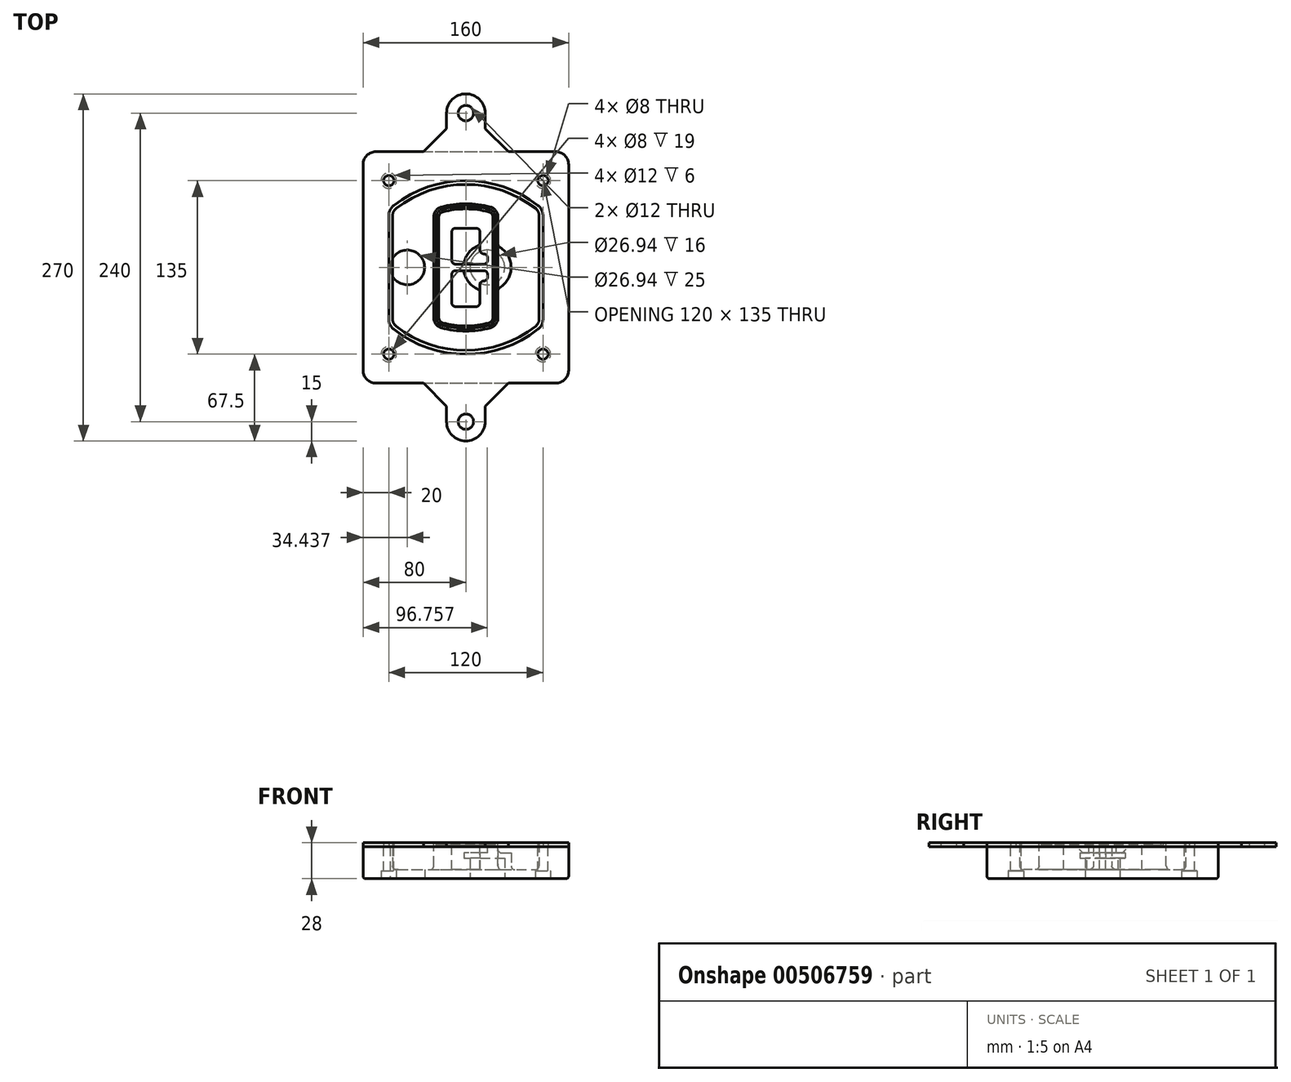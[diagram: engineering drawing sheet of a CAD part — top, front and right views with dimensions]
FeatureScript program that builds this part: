
annotation { "Feature Type Name" : "Feature", "Feature Type Description" : "" }
export const myFeature = defineFeature(function(context is Context, id is Id, definition is map)
    precondition{}
    {
        {
            var Q0;
            Q0=qCreatedBy(makeId("Top.planeOp"),FACE);
            var sketch = newSketch(context, id + "F0", { "sketchPlane" : qUnion([Q0])});
            skPoint(sketch, "E0.rect.middle", {"position": v(0, 0) * mm});
            skLineSegment(sketch, "E1.bottom", {"start": v(-70, -90) * mm, "end": v(70, -90) * mm});
            skLineSegment(sketch, "E1.top", {"start": v(-70, 90) * mm, "end": v(70, 90) * mm});
            skLineSegment(sketch, "E1.left", {"start": v(-80, -80) * mm, "end": v(-80, 80) * mm});
            skLineSegment(sketch, "E1.right", {"start": v(80, -80) * mm, "end": v(80, 80) * mm});
            skLineSegment(sketch, "E2", {"start": v(-80, 90) * mm, "end": v(80, -90) * mm, "construction": true});
            skLineSegment(sketch, "E3", {"start": v(80, 90) * mm, "end": v(-80, -90) * mm, "construction": true});
            skCircle(sketch, "E4", {"center": v(-60, 67.5) * mm, "radius": 4 * mm});
            skCircle(sketch, "E5", {"center": v(60, 67.5) * mm, "radius": 4 * mm});
            skCircle(sketch, "E6", {"center": v(60, -67.5) * mm, "radius": 4 * mm});
            skCircle(sketch, "E7", {"center": v(-60, -67.5) * mm, "radius": 4 * mm});
            skLineSegment(sketch, "E8", {"start": v(-60, 67.5) * mm, "end": v(60, 67.5) * mm, "construction": true});
            skLineSegment(sketch, "E9", {"start": v(60, 67.5) * mm, "end": v(60, -67.5) * mm, "construction": true});
            skLineSegment(sketch, "E10", {"start": v(60, -67.5) * mm, "end": v(-60, -67.5) * mm, "construction": true});
            skLineSegment(sketch, "E11", {"start": v(-60, -67.5) * mm, "end": v(-60, 67.5) * mm, "construction": true});
            skLineSegment(sketch, "E12", {"start": v(-60, 40.3) * mm, "end": v(-60, -40.3) * mm});
            skLineSegment(sketch, "E13", {"start": v(60, 40.3) * mm, "end": v(60, -40.3) * mm});
            skArc(sketch, "E14", {"start": v(56.15, 48.18) * mm, "mid": v(0, 67.5) * mm, "end": v(-56.15, 48.18) * mm});
            skArc(sketch, "E15", {"start": v(-56.15, -48.18) * mm, "mid": v(0, -67.5) * mm, "end": v(56.15, -48.18) * mm});
            skLineSegment(sketch, "E16", {"start": v(-60, 0) * mm, "end": v(60, 0) * mm, "construction": true});
            skPoint(sketch, "E17.visualSharp", {"position": v(-60, -45) * mm});
            skArc(sketch, "E17.filletArc", {"start": v(-60, -40.3) * mm, "mid": v(-58.99, -44.68) * mm, "end": v(-56.15, -48.18) * mm});
            skPoint(sketch, "E18.visualSharp", {"position": v(-60, 45) * mm});
            skArc(sketch, "E18.filletArc", {"start": v(-56.15, 48.18) * mm, "mid": v(-58.99, 44.68) * mm, "end": v(-60, 40.3) * mm});
            skPoint(sketch, "E19.visualSharp", {"position": v(60, 45) * mm});
            skArc(sketch, "E19.filletArc", {"start": v(60, 40.3) * mm, "mid": v(58.99, 44.68) * mm, "end": v(56.15, 48.18) * mm});
            skPoint(sketch, "E20.visualSharp", {"position": v(60, -45) * mm});
            skArc(sketch, "E20.filletArc", {"start": v(56.15, -48.18) * mm, "mid": v(58.99, -44.68) * mm, "end": v(60, -40.3) * mm});
            skPoint(sketch, "E21.visualSharp", {"position": v(-80, 90) * mm});
            skArc(sketch, "E21.filletArc", {"start": v(-70, 90) * mm, "mid": v(-77.07, 87.07) * mm, "end": v(-80, 80) * mm});
            skPoint(sketch, "E22.visualSharp", {"position": v(80, 90) * mm});
            skArc(sketch, "E22.filletArc", {"start": v(80, 80) * mm, "mid": v(77.07, 87.07) * mm, "end": v(70, 90) * mm});
            skPoint(sketch, "E23.visualSharp", {"position": v(80, -90) * mm});
            skArc(sketch, "E23.filletArc", {"start": v(70, -90) * mm, "mid": v(77.07, -87.07) * mm, "end": v(80, -80) * mm});
            skPoint(sketch, "E24.visualSharp", {"position": v(-80, -90) * mm});
            skArc(sketch, "E24.filletArc", {"start": v(-80, -80) * mm, "mid": v(-77.07, -87.07) * mm, "end": v(-70, -90) * mm});
            skArc(sketch, "E25.0", {"start": v(57, 40.3) * mm, "mid": v(56.3, 43.36) * mm, "end": v(54.3, 45.81) * mm});
            skLineSegment(sketch, "E25.1", {"start": v(57, 40.3) * mm, "end": v(57, -40.3) * mm});
            skArc(sketch, "E25.2", {"start": v(54.3, -45.81) * mm, "mid": v(56.3, -43.36) * mm, "end": v(57, -40.3) * mm});
            skArc(sketch, "E25.3", {"start": v(-54.3, -45.81) * mm, "mid": v(0, -64.5) * mm, "end": v(54.3, -45.81) * mm});
            skArc(sketch, "E25.4", {"start": v(-57, -40.3) * mm, "mid": v(-56.3, -43.36) * mm, "end": v(-54.3, -45.81) * mm});
            skArc(sketch, "E25.5", {"start": v(54.3, 45.81) * mm, "mid": v(0, 64.5) * mm, "end": v(-54.3, 45.81) * mm});
            skLineSegment(sketch, "E25.6", {"start": v(-57, 40.3) * mm, "end": v(-57, -40.3) * mm});
            skArc(sketch, "E25.7", {"start": v(-54.3, 45.81) * mm, "mid": v(-56.3, 43.36) * mm, "end": v(-57, 40.3) * mm});
            skArc(sketch, "E26.0", {"start": v(-58.62, 51.33) * mm, "mid": v(-62.58, 46.43) * mm, "end": v(-64, 40.3) * mm});
            skArc(sketch, "E26.1", {"start": v(58.62, 51.33) * mm, "mid": v(0, 71.5) * mm, "end": v(-58.62, 51.33) * mm});
            skArc(sketch, "E26.2", {"start": v(64, 40.3) * mm, "mid": v(62.58, 46.43) * mm, "end": v(58.62, 51.33) * mm});
            skLineSegment(sketch, "E26.3", {"start": v(64, 40.3) * mm, "end": v(64, -40.3) * mm});
            skArc(sketch, "E26.4", {"start": v(58.62, -51.33) * mm, "mid": v(62.58, -46.43) * mm, "end": v(64, -40.3) * mm});
            skLineSegment(sketch, "E26.5", {"start": v(-64, 40.3) * mm, "end": v(-64, -40.3) * mm});
            skArc(sketch, "E26.6", {"start": v(-58.62, -51.33) * mm, "mid": v(0, -71.5) * mm, "end": v(58.62, -51.33) * mm});
            skArc(sketch, "E26.7", {"start": v(-64, -40.3) * mm, "mid": v(-62.58, -46.43) * mm, "end": v(-58.62, -51.33) * mm});
            skSolve(sketch);
        }
        {
            var Q0;
            Q0=makeQuery(id+"F0.imprint","IMPRINT",FACE,{"disambiguationData":[TD([[makeQuery(id+"F0.imprint","IMPRINT",EDGE,{"derivedFrom":sQuery(id+"F0.wireOp",EDGE,"E1.bottom")}),1.0]])]});
            var Q1;
            Q1=makeQuery(id+"F0.imprint","IMPRINT",FACE,{"disambiguationData":[TD([[makeQuery(id+"F0.imprint","IMPRINT",EDGE,{"derivedFrom":sQuery(id+"F0.wireOp",EDGE,"E12")}),1.0]])]});
            var Q2;
            Q2=makeQuery(id+"F0.imprint","IMPRINT",FACE,{"disambiguationData":[TD([[makeQuery(id+"F0.imprint","IMPRINT",EDGE,{"derivedFrom":sQuery(id+"F0.wireOp",EDGE,"E25.0")}),1.0]])]});
            var Q3;
            Q3=makeQuery(id+"F0.imprint","IMPRINT",FACE,{"disambiguationData":[TD([[makeQuery(id+"F0.imprint","IMPRINT",EDGE,{"derivedFrom":sQuery(id+"F0.wireOp",EDGE,"E12")}),-1.0]])]});
            extrude(context, id + "F1", {"entities" : qUnion([Q0, Q1, Q2, Q3]), "oppositeDirection" : true, "depth" : 25 * mm});
        }
        {
            var Q0;
            Q0=makeQuery(id+"F0.imprint","IMPRINT",FACE,{"disambiguationData":[TD([[makeQuery(id+"F0.imprint","IMPRINT",EDGE,{"derivedFrom":sQuery(id+"F0.wireOp",EDGE,"E12")}),1.0]])]});
            extrude(context, id + "F2", {"entities" : qUnion([Q0]), "operationType" : NewBodyOperationType.ADD, "depth" : 3 * mm});
        }
        {
            var Q0;
            Q0=makeQuery(id+"F0.imprint","IMPRINT",FACE,{"disambiguationData":[TD([[makeQuery(id+"F0.imprint","IMPRINT",EDGE,{"derivedFrom":sQuery(id+"F0.wireOp",EDGE,"E25.0")}),1.0]])]});
            extrude(context, id + "F3", {"entities" : qUnion([Q0]), "operationType" : NewBodyOperationType.REMOVE, "oppositeDirection" : true, "depth" : 18 * mm});
        }
        {
            var Q0;
            Q0=makeQuery(id+"F2.opExtrude","CAP_FACE",FACE,{"disambiguationData":[OSD([sQuery(id+"F0.wireOp",EDGE,"E12"),sQuery(id+"F0.wireOp",EDGE,"E13"),sQuery(id+"F0.wireOp",EDGE,"E14"),sQuery(id+"F0.wireOp",EDGE,"E15"),sQuery(id+"F0.wireOp",EDGE,"E17.filletArc"),sQuery(id+"F0.wireOp",EDGE,"E18.filletArc"),sQuery(id+"F0.wireOp",EDGE,"E19.filletArc"),sQuery(id+"F0.wireOp",EDGE,"E20.filletArc"),sQuery(id+"F0.wireOp",EDGE,"E25.0"),sQuery(id+"F0.wireOp",EDGE,"E25.1"),sQuery(id+"F0.wireOp",EDGE,"E25.2"),sQuery(id+"F0.wireOp",EDGE,"E25.3"),sQuery(id+"F0.wireOp",EDGE,"E25.4"),sQuery(id+"F0.wireOp",EDGE,"E25.5"),sQuery(id+"F0.wireOp",EDGE,"E25.6"),sQuery(id+"F0.wireOp",EDGE,"E25.7")])],"isStart":false});
            var sketch = newSketch(context, id + "F4", { "sketchPlane" : qUnion([Q0])});
            skArc(sketch, "E27.0", {"start": v(-19.08, -46.97) * mm, "mid": v(0, -49.5) * mm, "end": v(19.08, -46.97) * mm});
            skArc(sketch, "E28.0", {"start": v(19.08, 46.97) * mm, "mid": v(0, 49.5) * mm, "end": v(-19.08, 46.97) * mm});
            skLineSegment(sketch, "E29", {"start": v(-25, 39.25) * mm, "end": v(-25, -39.25) * mm});
            skLineSegment(sketch, "E30", {"start": v(25, 39.25) * mm, "end": v(25, -39.25) * mm});
            skLineSegment(sketch, "E31", {"start": v(-25, 45.1) * mm, "end": v(25, 45.1) * mm, "construction": true});
            skLineSegment(sketch, "E32", {"start": v(-25, -45.1) * mm, "end": v(25, -45.1) * mm, "construction": true});
            skPoint(sketch, "E33.visualSharp", {"position": v(-25, 45.1) * mm});
            skArc(sketch, "E33.filletArc", {"start": v(-19.08, 46.97) * mm, "mid": v(-23.35, 44.11) * mm, "end": v(-25, 39.25) * mm});
            skPoint(sketch, "E34.visualSharp", {"position": v(25, 45.1) * mm});
            skArc(sketch, "E34.filletArc", {"start": v(25, 39.25) * mm, "mid": v(23.35, 44.11) * mm, "end": v(19.08, 46.97) * mm});
            skPoint(sketch, "E35.visualSharp", {"position": v(25, -45.1) * mm});
            skArc(sketch, "E35.filletArc", {"start": v(19.08, -46.97) * mm, "mid": v(23.35, -44.11) * mm, "end": v(25, -39.25) * mm});
            skPoint(sketch, "E36.visualSharp", {"position": v(-25, -45.1) * mm});
            skArc(sketch, "E36.filletArc", {"start": v(-25, -39.25) * mm, "mid": v(-23.35, -44.11) * mm, "end": v(-19.08, -46.97) * mm});
            skArc(sketch, "E37.0", {"start": v(54.3, 45.81) * mm, "mid": v(0, 64.5) * mm, "end": v(-54.3, 45.81) * mm});
            skArc(sketch, "E37.1", {"start": v(-54.3, 45.81) * mm, "mid": v(-56.3, 43.36) * mm, "end": v(-57, 40.3) * mm});
            skLineSegment(sketch, "E37.2", {"start": v(-57, 40.3) * mm, "end": v(-57, -40.3) * mm});
            skArc(sketch, "E37.3", {"start": v(-57, -40.3) * mm, "mid": v(-56.3, -43.36) * mm, "end": v(-54.3, -45.81) * mm});
            skArc(sketch, "E37.4", {"start": v(-54.3, -45.81) * mm, "mid": v(0, -64.5) * mm, "end": v(54.3, -45.81) * mm});
            skArc(sketch, "E37.5", {"start": v(54.3, -45.81) * mm, "mid": v(56.3, -43.36) * mm, "end": v(57, -40.3) * mm});
            skLineSegment(sketch, "E37.6", {"start": v(57, 40.3) * mm, "end": v(57, -40.3) * mm});
            skArc(sketch, "E37.7", {"start": v(57, 40.3) * mm, "mid": v(56.3, 43.36) * mm, "end": v(54.3, 45.81) * mm});
            skLineSegment(sketch, "E38.0", {"start": v(23, 39.25) * mm, "end": v(23, -39.25) * mm});
            skArc(sketch, "E38.1", {"start": v(18.56, -45.04) * mm, "mid": v(21.76, -42.9) * mm, "end": v(23, -39.25) * mm});
            skArc(sketch, "E38.2", {"start": v(-18.56, -45.04) * mm, "mid": v(0, -47.5) * mm, "end": v(18.56, -45.04) * mm});
            skArc(sketch, "E38.3", {"start": v(-23, -39.25) * mm, "mid": v(-21.76, -42.9) * mm, "end": v(-18.56, -45.04) * mm});
            skLineSegment(sketch, "E38.4", {"start": v(-23, 39.25) * mm, "end": v(-23, -39.25) * mm});
            skArc(sketch, "E38.5", {"start": v(23, 39.25) * mm, "mid": v(21.76, 42.9) * mm, "end": v(18.56, 45.04) * mm});
            skArc(sketch, "E38.6", {"start": v(-18.56, 45.04) * mm, "mid": v(-21.76, 42.9) * mm, "end": v(-23, 39.25) * mm});
            skArc(sketch, "E38.7", {"start": v(18.56, 45.04) * mm, "mid": v(0, 47.5) * mm, "end": v(-18.56, 45.04) * mm});
            skArc(sketch, "E39.0", {"start": v(21, 39.25) * mm, "mid": v(20.18, 41.68) * mm, "end": v(18.04, 43.1) * mm});
            skLineSegment(sketch, "E39.1", {"start": v(21, 39.25) * mm, "end": v(21, -39.25) * mm});
            skArc(sketch, "E39.2", {"start": v(18.04, -43.1) * mm, "mid": v(20.18, -41.68) * mm, "end": v(21, -39.25) * mm});
            skArc(sketch, "E39.3", {"start": v(-18.04, -43.1) * mm, "mid": v(0, -45.5) * mm, "end": v(18.04, -43.1) * mm});
            skArc(sketch, "E39.4", {"start": v(-21, -39.25) * mm, "mid": v(-20.18, -41.68) * mm, "end": v(-18.04, -43.1) * mm});
            skArc(sketch, "E39.5", {"start": v(18.04, 43.1) * mm, "mid": v(0, 45.5) * mm, "end": v(-18.04, 43.1) * mm});
            skLineSegment(sketch, "E39.6", {"start": v(-21, 39.25) * mm, "end": v(-21, -39.25) * mm});
            skArc(sketch, "E39.7", {"start": v(-18.04, 43.1) * mm, "mid": v(-20.18, 41.68) * mm, "end": v(-21, 39.25) * mm});
            skLineSegment(sketch, "E40", {"start": v(-25, 0) * mm, "end": v(25, 0) * mm, "construction": true});
            skLineSegment(sketch, "E41", {"start": v(-11, 5.5) * mm, "end": v(-11, 27.5) * mm});
            skLineSegment(sketch, "E42", {"start": v(-8, 30.5) * mm, "end": v(8, 30.5) * mm});
            skLineSegment(sketch, "E43", {"start": v(11, 27.5) * mm, "end": v(11, 13.5) * mm});
            skLineSegment(sketch, "E44", {"start": v(14, 10.5) * mm, "end": v(14, 10.5) * mm});
            skLineSegment(sketch, "E45", {"start": v(17, 7.5) * mm, "end": v(17, 5.5) * mm});
            skLineSegment(sketch, "E46", {"start": v(14, 2.5) * mm, "end": v(-8, 2.5) * mm});
            skPoint(sketch, "E47.visualSharp", {"position": v(-11, 30.5) * mm});
            skArc(sketch, "E47.filletArc", {"start": v(-8, 30.5) * mm, "mid": v(-10.12, 29.62) * mm, "end": v(-11, 27.5) * mm});
            skPoint(sketch, "E48.visualSharp", {"position": v(11, 30.5) * mm});
            skArc(sketch, "E48.filletArc", {"start": v(11, 27.5) * mm, "mid": v(10.12, 29.62) * mm, "end": v(8, 30.5) * mm});
            skPoint(sketch, "E49.visualSharp", {"position": v(11, 10.5) * mm});
            skArc(sketch, "E49.filletArc", {"start": v(11, 13.5) * mm, "mid": v(11.88, 11.38) * mm, "end": v(14, 10.5) * mm});
            skPoint(sketch, "E50.visualSharp", {"position": v(17, 10.5) * mm});
            skArc(sketch, "E50.filletArc", {"start": v(17, 7.5) * mm, "mid": v(16.12, 9.62) * mm, "end": v(14, 10.5) * mm});
            skPoint(sketch, "E51.visualSharp", {"position": v(17, 2.5) * mm});
            skArc(sketch, "E51.filletArc", {"start": v(14, 2.5) * mm, "mid": v(16.12, 3.38) * mm, "end": v(17, 5.5) * mm});
            skPoint(sketch, "E52.visualSharp", {"position": v(-11, 2.5) * mm});
            skArc(sketch, "E52.filletArc", {"start": v(-11, 5.5) * mm, "mid": v(-10.12, 3.38) * mm, "end": v(-8, 2.5) * mm});
            skLineSegment(sketch, "E53.0.MirrorCS", {"start": v(14, -2.5) * mm, "end": v(-8, -2.5) * mm});
            skArc(sketch, "E54.0.MirrorCS", {"start": v(-11, -5.5) * mm, "mid": v(-10.12, -3.38) * mm, "end": v(-8, -2.5) * mm});
            skLineSegment(sketch, "E55.0.MirrorCS", {"start": v(-11, -5.5) * mm, "end": v(-11, -27.5) * mm});
            skArc(sketch, "E56.0.MirrorCS", {"start": v(-8, -30.5) * mm, "mid": v(-10.12, -29.62) * mm, "end": v(-11, -27.5) * mm});
            skLineSegment(sketch, "E57.0.MirrorCS", {"start": v(-8, -30.5) * mm, "end": v(8, -30.5) * mm});
            skArc(sketch, "E58.0.MirrorCS", {"start": v(11, -27.5) * mm, "mid": v(10.12, -29.62) * mm, "end": v(8, -30.5) * mm});
            skLineSegment(sketch, "E59.0.MirrorCS", {"start": v(11, -27.5) * mm, "end": v(11, -13.5) * mm});
            skArc(sketch, "E60.0.MirrorCS", {"start": v(11, -13.5) * mm, "mid": v(11.88, -11.38) * mm, "end": v(14, -10.5) * mm});
            skArc(sketch, "E61.0.MirrorCS", {"start": v(17, -7.5) * mm, "mid": v(16.12, -9.62) * mm, "end": v(14, -10.5) * mm});
            skLineSegment(sketch, "E62.0.MirrorCS", {"start": v(17, -7.5) * mm, "end": v(17, -5.5) * mm});
            skArc(sketch, "E63.0.MirrorCS", {"start": v(14, -2.5) * mm, "mid": v(16.12, -3.38) * mm, "end": v(17, -5.5) * mm});
            skSolve(sketch);
        }
        {
            var Q0;
            Q0=makeQuery(id+"F4.imprint","IMPRINT",FACE,{"disambiguationData":[TD([[makeQuery(id+"F4.imprint","IMPRINT",EDGE,{"derivedFrom":sQuery(id+"F4.wireOp",EDGE,"E27.0")}),1.0]])]});
            var Q1;
            Q1=makeQuery(id+"F4.imprint","IMPRINT",FACE,{"disambiguationData":[TD([[makeQuery(id+"F4.imprint","IMPRINT",EDGE,{"derivedFrom":sQuery(id+"F4.wireOp",EDGE,"E38.0")}),-1.0]])]});
            var Q2;
            Q2=makeQuery(id+"F4.imprint","IMPRINT",FACE,{"disambiguationData":[TD([[makeQuery(id+"F4.imprint","IMPRINT",EDGE,{"derivedFrom":sQuery(id+"F4.wireOp",EDGE,"E39.0")}),1.0]])]});
            extrude(context, id + "F5", {"entities" : qUnion([Q0, Q1, Q2]), "operationType" : NewBodyOperationType.ADD, "endBound" : BoundingType.UP_TO_NEXT, "oppositeDirection" : true, "depth" : 25 * mm});
        }
        {
            var Q0;
            Q0=makeQuery(id+"F4.imprint","IMPRINT",FACE,{"disambiguationData":[TD([[makeQuery(id+"F4.imprint","IMPRINT",EDGE,{"derivedFrom":sQuery(id+"F4.wireOp",EDGE,"E38.0")}),-1.0]])]});
            extrude(context, id + "F6", {"entities" : qUnion([Q0]), "operationType" : NewBodyOperationType.REMOVE, "oppositeDirection" : true, "depth" : 2 * mm});
        }
        {
            var Q0;
            Q0=makeQuery(id+"F1.opExtrude","CAP_FACE",FACE,{"disambiguationData":[OSD([sQuery(id+"F0.wireOp",EDGE,"E1.bottom"),sQuery(id+"F0.wireOp",EDGE,"E1.top"),sQuery(id+"F0.wireOp",EDGE,"E1.left"),sQuery(id+"F0.wireOp",EDGE,"E1.right"),sQuery(id+"F0.wireOp",EDGE,"E4"),sQuery(id+"F0.wireOp",EDGE,"E5"),sQuery(id+"F0.wireOp",EDGE,"E6"),sQuery(id+"F0.wireOp",EDGE,"E7"),sQuery(id+"F0.wireOp",EDGE,"E21.filletArc"),sQuery(id+"F0.wireOp",EDGE,"E22.filletArc"),sQuery(id+"F0.wireOp",EDGE,"E23.filletArc"),sQuery(id+"F0.wireOp",EDGE,"E24.filletArc")])],"isStart":false});
            var sketch = newSketch(context, id + "F7", { "sketchPlane" : qUnion([Q0])});
            skCircle(sketch, "E64", {"center": v(16.76, 0) * mm, "radius": 13.47 * mm});
            skCircle(sketch, "E65", {"center": v(-45.56, 0) * mm, "radius": 13.47 * mm});
            skLineSegment(sketch, "E66", {"start": v(80, 0) * mm, "end": v(-80, 0) * mm});
            skCircle(sketch, "E67", {"center": v(16.76, 0) * mm, "radius": 18.47 * mm});
            skCircle(sketch, "E68", {"center": v(60, -67.5) * mm, "radius": 6 * mm});
            skCircle(sketch, "E69", {"center": v(-60, -67.5) * mm, "radius": 6 * mm});
            skCircle(sketch, "E70", {"center": v(-60, 67.5) * mm, "radius": 6 * mm});
            skCircle(sketch, "E71", {"center": v(60, 67.5) * mm, "radius": 6 * mm});
            skSolve(sketch);
        }
        {
            var Q0;
            {var subQ1=sQuery(id+"F7.wireOp",EDGE,"E66");var subQ4=sQuery(id+"F7.wireOp",EDGE,"E64");var subQ6=makeQuery(id+"F7.imprint","INTERSECT",VERTEX,{"disambiguationData":[OD(0.0)],"derivedFrom":[subQ4,subQ1]});Q0=makeQuery(id+"F7.imprint","IMPRINT",FACE,{"disambiguationData":[TD([[makeQuery(id+"F7.imprint","IMPRINT",EDGE,{"disambiguationData":[TD([[subQ6,-1.0]])],"derivedFrom":subQ4}),-1.0]])]});}
            var Q1;
            {var subQ0=sQuery(id+"F7.wireOp",EDGE,"E66");var subQ1=sQuery(id+"F7.wireOp",EDGE,"E64");var subQ3=makeQuery(id+"F7.imprint","INTERSECT",VERTEX,{"disambiguationData":[OD(0.0)],"derivedFrom":[subQ1,subQ0]});Q1=makeQuery(id+"F7.imprint","IMPRINT",FACE,{"disambiguationData":[TD([[makeQuery(id+"F7.imprint","IMPRINT",EDGE,{"disambiguationData":[TD([[subQ3,-1.0]])],"derivedFrom":subQ1}),1.0]])]});}
            var Q2;
            {var subQ0=sQuery(id+"F7.wireOp",EDGE,"E66");var subQ1=sQuery(id+"F7.wireOp",EDGE,"E64");var subQ3=makeQuery(id+"F7.imprint","INTERSECT",VERTEX,{"disambiguationData":[OD(0.0)],"derivedFrom":[subQ1,subQ0]});Q2=makeQuery(id+"F7.imprint","IMPRINT",FACE,{"disambiguationData":[TD([[makeQuery(id+"F7.imprint","IMPRINT",EDGE,{"disambiguationData":[TD([[subQ3,1.0]])],"derivedFrom":subQ1}),1.0]])]});}
            var Q3;
            {var subQ1=sQuery(id+"F7.wireOp",EDGE,"E66");var subQ4=sQuery(id+"F7.wireOp",EDGE,"E64");var subQ6=makeQuery(id+"F7.imprint","INTERSECT",VERTEX,{"disambiguationData":[OD(0.0)],"derivedFrom":[subQ4,subQ1]});Q3=makeQuery(id+"F7.imprint","IMPRINT",FACE,{"disambiguationData":[TD([[makeQuery(id+"F7.imprint","IMPRINT",EDGE,{"disambiguationData":[TD([[subQ6,1.0]])],"derivedFrom":subQ4}),-1.0]])]});}
            extrude(context, id + "F8", {"entities" : qUnion([Q0, Q1, Q2, Q3]), "operationType" : NewBodyOperationType.ADD, "oppositeDirection" : true, "depth" : 20 * mm});
        }
        {
            var Q0;
            {var subQ0=sQuery(id+"F7.wireOp",EDGE,"E66");var subQ1=sQuery(id+"F7.wireOp",EDGE,"E64");var subQ3=makeQuery(id+"F7.imprint","INTERSECT",VERTEX,{"disambiguationData":[OD(0.0)],"derivedFrom":[subQ1,subQ0]});Q0=makeQuery(id+"F7.imprint","IMPRINT",FACE,{"disambiguationData":[TD([[makeQuery(id+"F7.imprint","IMPRINT",EDGE,{"disambiguationData":[TD([[subQ3,-1.0]])],"derivedFrom":subQ1}),1.0]])]});}
            var Q1;
            {var subQ0=sQuery(id+"F7.wireOp",EDGE,"E66");var subQ1=sQuery(id+"F7.wireOp",EDGE,"E64");var subQ3=makeQuery(id+"F7.imprint","INTERSECT",VERTEX,{"disambiguationData":[OD(0.0)],"derivedFrom":[subQ1,subQ0]});Q1=makeQuery(id+"F7.imprint","IMPRINT",FACE,{"disambiguationData":[TD([[makeQuery(id+"F7.imprint","IMPRINT",EDGE,{"disambiguationData":[TD([[subQ3,1.0]])],"derivedFrom":subQ1}),1.0]])]});}
            extrude(context, id + "F9", {"entities" : qUnion([Q0, Q1]), "operationType" : NewBodyOperationType.REMOVE, "oppositeDirection" : true, "depth" : 16 * mm});
        }
        {
            var Q0;
            {var subQ0=sQuery(id+"F7.wireOp",EDGE,"E66");var subQ1=sQuery(id+"F7.wireOp",EDGE,"E65");var subQ3=makeQuery(id+"F7.imprint","INTERSECT",VERTEX,{"disambiguationData":[OD(0.0)],"derivedFrom":[subQ1,subQ0]});Q0=makeQuery(id+"F7.imprint","IMPRINT",FACE,{"disambiguationData":[TD([[makeQuery(id+"F7.imprint","IMPRINT",EDGE,{"disambiguationData":[TD([[subQ3,-1.0]])],"derivedFrom":subQ1}),1.0]])]});}
            var Q1;
            {var subQ0=sQuery(id+"F7.wireOp",EDGE,"E66");var subQ1=sQuery(id+"F7.wireOp",EDGE,"E65");var subQ3=makeQuery(id+"F7.imprint","INTERSECT",VERTEX,{"disambiguationData":[OD(0.0)],"derivedFrom":[subQ1,subQ0]});Q1=makeQuery(id+"F7.imprint","IMPRINT",FACE,{"disambiguationData":[TD([[makeQuery(id+"F7.imprint","IMPRINT",EDGE,{"disambiguationData":[TD([[subQ3,1.0]])],"derivedFrom":subQ1}),1.0]])]});}
            extrude(context, id + "F10", {"entities" : qUnion([Q0, Q1]), "operationType" : NewBodyOperationType.REMOVE, "oppositeDirection" : true, "depth" : 25 * mm});
        }
        {
            var Q0;
            Q0=makeQuery(id+"F7.imprint","IMPRINT",FACE,{"disambiguationData":[TD([[makeQuery(id+"F7.imprint","IMPRINT",EDGE,{"derivedFrom":sQuery(id+"F7.wireOp",EDGE,"E68")}),1.0]])]});
            var Q1;
            Q1=makeQuery(id+"F7.imprint","IMPRINT",FACE,{"disambiguationData":[TD([[makeQuery(id+"F7.imprint","IMPRINT",EDGE,{"derivedFrom":makeQuery(id+"F1.opExtrude","CAP_EDGE",EDGE,{"disambiguationData":[OSD([sQuery(id+"F0.wireOp",EDGE,"E5")])],"isStart":false})}),-1.0]])]});
            var Q2;
            Q2=makeQuery(id+"F7.imprint","IMPRINT",FACE,{"disambiguationData":[TD([[makeQuery(id+"F7.imprint","IMPRINT",EDGE,{"derivedFrom":sQuery(id+"F7.wireOp",EDGE,"E69")}),1.0]])]});
            var Q3;
            Q3=makeQuery(id+"F7.imprint","IMPRINT",FACE,{"disambiguationData":[TD([[makeQuery(id+"F7.imprint","IMPRINT",EDGE,{"derivedFrom":makeQuery(id+"F1.opExtrude","CAP_EDGE",EDGE,{"disambiguationData":[OSD([sQuery(id+"F0.wireOp",EDGE,"E4")])],"isStart":false})}),-1.0]])]});
            var Q4;
            Q4=makeQuery(id+"F7.imprint","IMPRINT",FACE,{"disambiguationData":[TD([[makeQuery(id+"F7.imprint","IMPRINT",EDGE,{"derivedFrom":sQuery(id+"F7.wireOp",EDGE,"E70")}),1.0]])]});
            var Q5;
            Q5=makeQuery(id+"F7.imprint","IMPRINT",FACE,{"disambiguationData":[TD([[makeQuery(id+"F7.imprint","IMPRINT",EDGE,{"derivedFrom":makeQuery(id+"F1.opExtrude","CAP_EDGE",EDGE,{"disambiguationData":[OSD([sQuery(id+"F0.wireOp",EDGE,"E7")])],"isStart":false})}),-1.0]])]});
            var Q6;
            Q6=makeQuery(id+"F7.imprint","IMPRINT",FACE,{"disambiguationData":[TD([[makeQuery(id+"F7.imprint","IMPRINT",EDGE,{"derivedFrom":sQuery(id+"F7.wireOp",EDGE,"E71")}),1.0]])]});
            var Q7;
            Q7=makeQuery(id+"F7.imprint","IMPRINT",FACE,{"disambiguationData":[TD([[makeQuery(id+"F7.imprint","IMPRINT",EDGE,{"derivedFrom":makeQuery(id+"F1.opExtrude","CAP_EDGE",EDGE,{"disambiguationData":[OSD([sQuery(id+"F0.wireOp",EDGE,"E6")])],"isStart":false})}),-1.0]])]});
            extrude(context, id + "F11", {"entities" : qUnion([Q0, Q1, Q2, Q3, Q4, Q5, Q6, Q7]), "operationType" : NewBodyOperationType.REMOVE, "oppositeDirection" : true, "depth" : 6 * mm});
        }
        {
            var Q0;
            Q0=makeQuery(id+"F9.boolean.opBoolean","COPY",FACE,{"derivedFrom":makeQuery(id+"F9.opExtrude","CAP_FACE",FACE,{"disambiguationData":[OSD([sQuery(id+"F7.wireOp",EDGE,"E64")])],"isStart":false})});
            var sketch = newSketch(context, id + "F12", { "sketchPlane" : qUnion([Q0])});
            skArc(sketch, "E72.0", {"start": v(11, 17.55) * mm, "mid": v(2.57, 11.82) * mm, "end": v(-1.54, 2.5) * mm});
            skArc(sketch, "E72.1", {"start": v(-1.54, -2.5) * mm, "mid": v(2.57, -11.82) * mm, "end": v(11, -17.55) * mm});
            skLineSegment(sketch, "E73", {"start": v(-1.54, -2.5) * mm, "end": v(14, -2.5) * mm});
            skLineSegment(sketch, "E74.0", {"start": v(14, 2.5) * mm, "end": v(-1.54, 2.5) * mm});
            skArc(sketch, "E74.1", {"start": v(14, 2.5) * mm, "mid": v(16.12, 3.38) * mm, "end": v(17, 5.5) * mm});
            skLineSegment(sketch, "E74.2", {"start": v(17, 7.5) * mm, "end": v(17, 5.5) * mm});
            skArc(sketch, "E74.3", {"start": v(17, 7.5) * mm, "mid": v(16.12, 9.62) * mm, "end": v(14, 10.5) * mm});
            skArc(sketch, "E74.4", {"start": v(11, 13.5) * mm, "mid": v(11.88, 11.38) * mm, "end": v(14, 10.5) * mm});
            skLineSegment(sketch, "E74.5", {"start": v(11, 17.55) * mm, "end": v(11, 13.5) * mm});
            skLineSegment(sketch, "E74.7", {"start": v(14, -2.5) * mm, "end": v(-1.54, -2.5) * mm});
            skArc(sketch, "E74.8", {"start": v(14, -2.5) * mm, "mid": v(16.12, -3.38) * mm, "end": v(17, -5.5) * mm});
            skLineSegment(sketch, "E74.9", {"start": v(17, -7.5) * mm, "end": v(17, -5.5) * mm});
            skArc(sketch, "E74.10", {"start": v(17, -7.5) * mm, "mid": v(16.12, -9.62) * mm, "end": v(14, -10.5) * mm});
            skArc(sketch, "E74.11", {"start": v(11, -13.5) * mm, "mid": v(11.88, -11.38) * mm, "end": v(14, -10.5) * mm});
            skLineSegment(sketch, "E74.12", {"start": v(11, -17.55) * mm, "end": v(11, -13.5) * mm});
            skPoint(sketch, "E75.orphan", {"position": v(11, -27.5) * mm});
            skPoint(sketch, "E76.orphan", {"position": v(-8, -2.5) * mm});
            skPoint(sketch, "E77.orphan", {"position": v(-8, 2.5) * mm});
            skPoint(sketch, "E78.orphan", {"position": v(11, 27.5) * mm});
            skSolve(sketch);
        }
        {
            var Q0;
            {var subQ7=sQuery(id+"F12.wireOp",EDGE,"E72.0");var subQ14=sQuery(id+"F12.wireOp",EDGE,"E72.1");var subQ16=sQuery(id+"F12.wireOp",EDGE,"E74.1");var subQ18=sQuery(id+"F12.wireOp",EDGE,"E74.8");Q0=qUnion([makeQuery(id+"F12.imprint","IMPRINT",FACE,{"disambiguationData":[TD([[makeQuery(id+"F12.imprint","IMPRINT",EDGE,{"derivedFrom":subQ7}),1.0]])]}),makeQuery(id+"F12.imprint","IMPRINT",FACE,{"disambiguationData":[TD([[makeQuery(id+"F12.imprint","IMPRINT",EDGE,{"derivedFrom":subQ14}),1.0]])]}),makeQuery(id+"F12.imprint","IMPRINT",FACE,{"disambiguationData":[TD([[makeQuery(id+"F12.imprint","IMPRINT",EDGE,{"derivedFrom":subQ16}),1.0]])]}),makeQuery(id+"F12.imprint","IMPRINT",FACE,{"disambiguationData":[TD([[makeQuery(id+"F12.imprint","IMPRINT",EDGE,{"derivedFrom":subQ18}),-1.0]])]})]);}
            var Q1;
            Q1=makeQuery(id+"F5.boolean.opBoolean","SPLIT",FACE,{"disambiguationData":[TD([makeQuery(id+"F5.opExtrude","SWEPT_FACE",FACE,{"disambiguationData":[OSD([sQuery(id+"F4.wireOp",EDGE,"E41")])]})])],"derivedFrom":makeQuery(id+"F3.boolean.opBoolean","COPY",FACE,{"derivedFrom":makeQuery(id+"F3.opExtrude","CAP_FACE",FACE,{"disambiguationData":[OSD([sQuery(id+"F0.wireOp",EDGE,"E25.0"),sQuery(id+"F0.wireOp",EDGE,"E25.1"),sQuery(id+"F0.wireOp",EDGE,"E25.2"),sQuery(id+"F0.wireOp",EDGE,"E25.3"),sQuery(id+"F0.wireOp",EDGE,"E25.4"),sQuery(id+"F0.wireOp",EDGE,"E25.5"),sQuery(id+"F0.wireOp",EDGE,"E25.6"),sQuery(id+"F0.wireOp",EDGE,"E25.7")])],"isStart":false})})});
            extrude(context, id + "F13", {"entities" : qUnion([Q0]), "operationType" : NewBodyOperationType.REMOVE, "endBound" : BoundingType.UP_TO_SURFACE, "endBoundEntityFace" : qUnion([Q1]), "depth" : 25 * mm});
        }
        {
            var Q0;
            Q0=makeQuery(id+"F3.boolean.opBoolean","COPY",EDGE,{"derivedFrom":makeQuery(id+"F3.opExtrude","CAP_EDGE",EDGE,{"disambiguationData":[OSD([sQuery(id+"F0.wireOp",EDGE,"E25.6")])],"isStart":false})});
            var Q1;
            Q1=makeQuery(id+"F8.boolean.opBoolean","INTERSECT",EDGE,{"derivedFrom":[makeQuery(id+"F5.opExtrude","SWEPT_FACE",FACE,{"disambiguationData":[OSD([sQuery(id+"F4.wireOp",EDGE,"E30")])]}),makeQuery(id+"F8.opExtrude","CAP_FACE",FACE,{"disambiguationData":[OSD([sQuery(id+"F7.wireOp",EDGE,"E67")])],"isStart":false})]});
            var Q2;
            Q2=makeQuery(id+"F8.boolean.opBoolean","INTERSECT",EDGE,{"disambiguationData":[OD(1.0)],"derivedFrom":[makeQuery(id+"F5.opExtrude","SWEPT_FACE",FACE,{"disambiguationData":[OSD([sQuery(id+"F4.wireOp",EDGE,"E30")])]}),makeQuery(id+"F8.opExtrude","SWEPT_FACE",FACE,{"disambiguationData":[OSD([sQuery(id+"F7.wireOp",EDGE,"E67")])]})]});
            var Q3;
            {var subQ0=sQuery(id+"F4.wireOp",EDGE,"E30");Q3=makeQuery(id+"F8.boolean.opBoolean","SPLIT",EDGE,{"disambiguationData":[TD([makeQuery(id+"F5.opExtrude","SWEPT_FACE",FACE,{"disambiguationData":[OSD([sQuery(id+"F4.wireOp",EDGE,"E35.filletArc")])]})])],"derivedFrom":makeQuery(id+"F5.opExtrude","CAP_EDGE",EDGE,{"disambiguationData":[OSD([subQ0])],"isStart":false})});}
            var Q4;
            {var subQ0=sQuery(id+"F0.wireOp",EDGE,"E25.7");var subQ1=sQuery(id+"F0.wireOp",EDGE,"E25.1");var subQ2=sQuery(id+"F0.wireOp",EDGE,"E25.6");var subQ3=sQuery(id+"F0.wireOp",EDGE,"E25.5");var subQ4=sQuery(id+"F0.wireOp",EDGE,"E25.4");var subQ5=sQuery(id+"F0.wireOp",EDGE,"E25.0");var subQ6=sQuery(id+"F0.wireOp",EDGE,"E25.2");var subQ7=sQuery(id+"F0.wireOp",EDGE,"E25.3");Q4=makeQuery(id+"F8.boolean.opBoolean","INTERSECT",EDGE,{"derivedFrom":[makeQuery(id+"F5.boolean.opBoolean","SPLIT",FACE,{"disambiguationData":[TD([makeQuery(id+"F2.opExtrude","SWEPT_FACE",FACE,{"disambiguationData":[OSD([subQ5])]})])],"derivedFrom":makeQuery(id+"F3.boolean.opBoolean","COPY",FACE,{"derivedFrom":makeQuery(id+"F3.opExtrude","CAP_FACE",FACE,{"disambiguationData":[OSD([subQ5,subQ1,subQ6,subQ7,subQ4,subQ3,subQ2,subQ0])],"isStart":false})})}),makeQuery(id+"F8.opExtrude","SWEPT_FACE",FACE,{"disambiguationData":[OSD([sQuery(id+"F7.wireOp",EDGE,"E67")])]})]});}
            var Q5;
            Q5=makeQuery(id+"F8.boolean.opBoolean","INTERSECT",EDGE,{"disambiguationData":[OD(0.0)],"derivedFrom":[makeQuery(id+"F5.opExtrude","SWEPT_FACE",FACE,{"disambiguationData":[OSD([sQuery(id+"F4.wireOp",EDGE,"E30")])]}),makeQuery(id+"F8.opExtrude","SWEPT_FACE",FACE,{"disambiguationData":[OSD([sQuery(id+"F7.wireOp",EDGE,"E67")])]})]});
            fillet(context, id + "F14", {"entities" : qUnion([Q0, Q1, Q2, Q3, Q4, Q5]), "radius" : 3 * mm, "tangentPropagation" : true, "allowEdgeOverflow" : false});
        }
        {
            var Q0;
            Q0=makeQuery(id+"F1.opExtrude","CAP_EDGE",EDGE,{"disambiguationData":[OSD([sQuery(id+"F0.wireOp",EDGE,"E1.bottom")])],"isStart":false});
            fillet(context, id + "F15", {"entities" : qUnion([Q0]), "radius" : 2 * mm, "tangentPropagation" : true, "allowEdgeOverflow" : false});
        }
        {
            var Q0;
            {var subQ0=sQuery(id+"F0.wireOp",EDGE,"E21.filletArc");var subQ1=sQuery(id+"F0.wireOp",EDGE,"E7");var subQ2=sQuery(id+"F0.wireOp",EDGE,"E6");var subQ3=sQuery(id+"F0.wireOp",EDGE,"E5");var subQ4=sQuery(id+"F0.wireOp",EDGE,"E4");var subQ5=sQuery(id+"F0.wireOp",EDGE,"E22.filletArc");var subQ6=sQuery(id+"F0.wireOp",EDGE,"E1.bottom");var subQ7=sQuery(id+"F0.wireOp",EDGE,"E1.right");var subQ8=sQuery(id+"F0.wireOp",EDGE,"E1.top");var subQ9=sQuery(id+"F0.wireOp",EDGE,"E1.left");var subQ10=sQuery(id+"F0.wireOp",EDGE,"E23.filletArc");var subQ11=sQuery(id+"F0.wireOp",EDGE,"E24.filletArc");Q0=makeQuery(id+"F2.boolean.opBoolean","SPLIT",FACE,{"disambiguationData":[TD([makeQuery(id+"F1.opExtrude","SWEPT_FACE",FACE,{"disambiguationData":[OSD([subQ6])]})])],"derivedFrom":makeQuery(id+"F1.opExtrude","CAP_FACE",FACE,{"disambiguationData":[OSD([subQ6,subQ8,subQ9,subQ7,subQ4,subQ3,subQ2,subQ1,subQ0,subQ5,subQ10,subQ11])],"isStart":true})});}
            var sketch = newSketch(context, id + "F16", { "sketchPlane" : qUnion([Q0])});
            skCircle(sketch, "E79.0", {"center": v(-60, 67.5) * mm, "radius": 4 * mm});
            skLineSegment(sketch, "E79.1", {"start": v(-70, 90) * mm, "end": v(70, 90) * mm});
            skArc(sketch, "E79.2", {"start": v(-70, 90) * mm, "mid": v(-77.07, 87.07) * mm, "end": v(-80, 80) * mm});
            skLineSegment(sketch, "E79.3", {"start": v(-80, -80) * mm, "end": v(-80, 80) * mm});
            skArc(sketch, "E79.4", {"start": v(56.15, 48.18) * mm, "mid": v(0, 67.5) * mm, "end": v(-56.15, 48.18) * mm});
            skLineSegment(sketch, "E79.5", {"start": v(-60, 40.3) * mm, "end": v(-60, -40.3) * mm});
            skCircle(sketch, "E79.6", {"center": v(60, 67.5) * mm, "radius": 4 * mm});
            skArc(sketch, "E79.7", {"start": v(80, 80) * mm, "mid": v(77.07, 87.07) * mm, "end": v(70, 90) * mm});
            skLineSegment(sketch, "E79.8", {"start": v(80, -80) * mm, "end": v(80, 80) * mm});
            skCircle(sketch, "E79.9", {"center": v(60, -67.5) * mm, "radius": 4 * mm});
            skCircle(sketch, "E79.10", {"center": v(-60, -67.5) * mm, "radius": 4 * mm});
            skArc(sketch, "E79.11", {"start": v(-80, -80) * mm, "mid": v(-77.07, -87.07) * mm, "end": v(-70, -90) * mm});
            skLineSegment(sketch, "E79.12", {"start": v(-70, -90) * mm, "end": v(70, -90) * mm});
            skArc(sketch, "E79.13", {"start": v(70, -90) * mm, "mid": v(77.07, -87.07) * mm, "end": v(80, -80) * mm});
            skArc(sketch, "E79.14", {"start": v(-56.15, -48.18) * mm, "mid": v(0, -67.5) * mm, "end": v(56.15, -48.18) * mm});
            skLineSegment(sketch, "E79.15", {"start": v(60, 40.3) * mm, "end": v(60, -40.3) * mm});
            skArc(sketch, "E79.16", {"start": v(60, 40.3) * mm, "mid": v(58.99, 44.68) * mm, "end": v(56.15, 48.18) * mm});
            skArc(sketch, "E79.17", {"start": v(-56.15, 48.18) * mm, "mid": v(-58.99, 44.68) * mm, "end": v(-60, 40.3) * mm});
            skArc(sketch, "E79.18", {"start": v(-60, -40.3) * mm, "mid": v(-58.99, -44.68) * mm, "end": v(-56.15, -48.18) * mm});
            skArc(sketch, "E79.19", {"start": v(56.15, -48.18) * mm, "mid": v(58.99, -44.68) * mm, "end": v(60, -40.3) * mm});
            skLineSegment(sketch, "E80", {"start": v(0, 90) * mm, "end": v(0, 120) * mm, "construction": true});
            skLineSegment(sketch, "E81", {"start": v(-33, 90) * mm, "end": v(-15, 108) * mm});
            skLineSegment(sketch, "E82", {"start": v(-15, 108) * mm, "end": v(-15, 120) * mm});
            skLineSegment(sketch, "E83", {"start": v(33, 90) * mm, "end": v(15, 108) * mm});
            skLineSegment(sketch, "E84", {"start": v(15, 108) * mm, "end": v(15, 120) * mm});
            skArc(sketch, "E85", {"start": v(15, 120) * mm, "mid": v(0, 135) * mm, "end": v(-15, 120) * mm});
            skCircle(sketch, "E86", {"center": v(0, 120) * mm, "radius": 6 * mm});
            skLineSegment(sketch, "E87", {"start": v(-80, 0) * mm, "end": v(80, 0) * mm, "construction": true});
            skLineSegment(sketch, "E88.MirrorCS", {"start": v(0, -90) * mm, "end": v(0, -120) * mm, "construction": true});
            skCircle(sketch, "E89.MirrorC", {"center": v(0, -120) * mm, "radius": 6 * mm});
            skArc(sketch, "E90.MirrorCS", {"start": v(15, -120) * mm, "mid": v(0, -135) * mm, "end": v(-15, -120) * mm});
            skLineSegment(sketch, "E91.MirrorCS", {"start": v(-15, -108) * mm, "end": v(-15, -120) * mm});
            skLineSegment(sketch, "E92.MirrorCS", {"start": v(-33, -90) * mm, "end": v(-15, -108) * mm});
            skLineSegment(sketch, "E93.MirrorCS", {"start": v(33, -90) * mm, "end": v(15, -108) * mm});
            skLineSegment(sketch, "E94.MirrorCS", {"start": v(15, -108) * mm, "end": v(15, -120) * mm});
            skSolve(sketch);
        }
        {
            var Q0;
            Q0 = qSketchRegion(id + "F16", true);
            var Q1;
            Q1=makeQuery(id+"F2.opExtrude","CAP_FACE",FACE,{"disambiguationData":[OSD([sQuery(id+"F0.wireOp",EDGE,"E12"),sQuery(id+"F0.wireOp",EDGE,"E13"),sQuery(id+"F0.wireOp",EDGE,"E14"),sQuery(id+"F0.wireOp",EDGE,"E15"),sQuery(id+"F0.wireOp",EDGE,"E17.filletArc"),sQuery(id+"F0.wireOp",EDGE,"E18.filletArc"),sQuery(id+"F0.wireOp",EDGE,"E19.filletArc"),sQuery(id+"F0.wireOp",EDGE,"E20.filletArc"),sQuery(id+"F0.wireOp",EDGE,"E25.0"),sQuery(id+"F0.wireOp",EDGE,"E25.1"),sQuery(id+"F0.wireOp",EDGE,"E25.2"),sQuery(id+"F0.wireOp",EDGE,"E25.3"),sQuery(id+"F0.wireOp",EDGE,"E25.4"),sQuery(id+"F0.wireOp",EDGE,"E25.5"),sQuery(id+"F0.wireOp",EDGE,"E25.6"),sQuery(id+"F0.wireOp",EDGE,"E25.7")])],"isStart":false});
            extrude(context, id + "F17", {"entities" : qUnion([Q0]), "endBound" : BoundingType.UP_TO_SURFACE, "endBoundEntityFace" : qUnion([Q1]), "depth" : 25 * mm});
        }
    });
